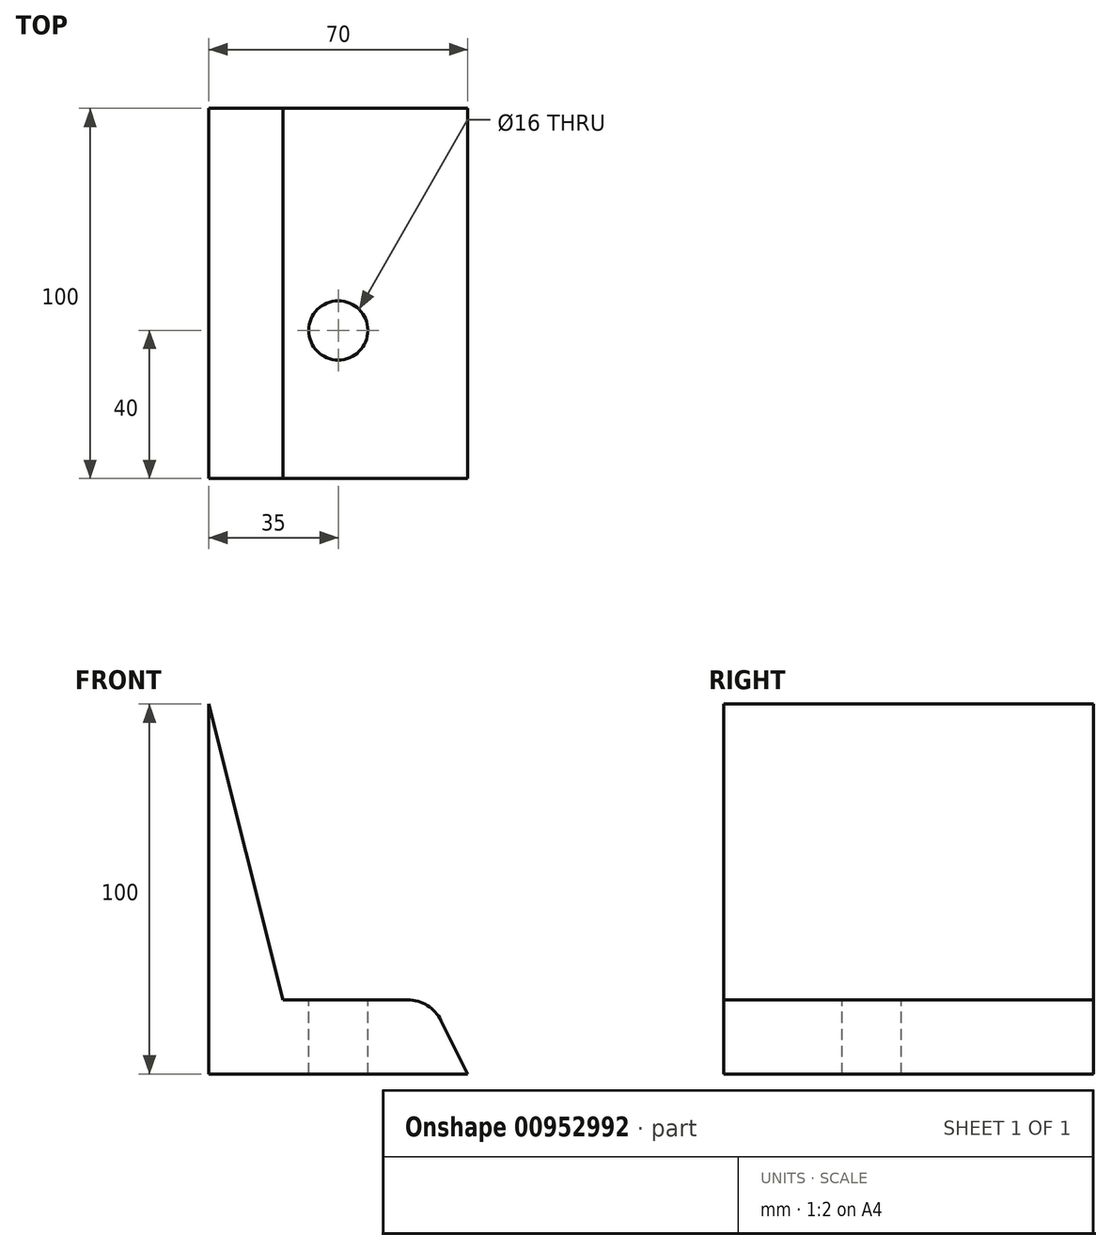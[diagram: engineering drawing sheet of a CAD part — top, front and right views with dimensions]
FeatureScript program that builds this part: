
annotation { "Feature Type Name" : "Feature", "Feature Type Description" : "" }
export const myFeature = defineFeature(function(context is Context, id is Id, definition is map)
    precondition{}
    {
        {
            var Q0;
            Q0=qCreatedBy(makeId("Front.planeOp"),FACE);
            var sketch = newSketch(context, id + "F0", { "sketchPlane" : qUnion([Q0])});
            skLineSegment(sketch, "E0", {"start": v(0, 0) * mm, "end": v(0, 100) * mm});
            skLineSegment(sketch, "E1", {"start": v(0, 100) * mm, "end": v(20, 20) * mm});
            skLineSegment(sketch, "E2", {"start": v(20, 20) * mm, "end": v(60, 20) * mm});
            skLineSegment(sketch, "E3", {"start": v(60, 20) * mm, "end": v(70, 0) * mm});
            skLineSegment(sketch, "E4", {"start": v(70, 0) * mm, "end": v(0, 0) * mm});
            skSolve(sketch);
        }
        {
            var Q0;
            Q0 = qSketchRegion(id + "F0", true);
            extrude(context, id + "F1", {"entities" : qUnion([Q0]), "oppositeDirection" : true, "depth" : 100 * mm, "offsetDistance" : 25 * mm});
        }
        {
            var Q0;
            Q0=makeQuery(id+"F1.opExtrude","SWEPT_EDGE",EDGE,{"disambiguationData":[OSD([sQuery(id+"F0.wireOp",EDGE,"E2"),sQuery(id+"F0.wireOp",EDGE,"E3")])]});
            fillet(context, id + "F2", {"entities" : qUnion([Q0]), "radius" : 10 * mm, "tangentPropagation" : true, "allowEdgeOverflow" : false});
        }
        {
            var Q0;
            Q0=makeQuery(id+"F1.opExtrude","SWEPT_FACE",FACE,{"disambiguationData":[OSD([sQuery(id+"F0.wireOp",EDGE,"E2")])]});
            var sketch = newSketch(context, id + "F3", { "sketchPlane" : qUnion([Q0])});
            skCircle(sketch, "E5", {"center": v(35, 40) * mm, "radius": 8 * mm});
            skSolve(sketch);
        }
        {
            var Q0;
            Q0 = qSketchRegion(id + "F3", true);
            extrude(context, id + "F4", {"entities" : qUnion([Q0]), "operationType" : NewBodyOperationType.REMOVE, "endBound" : BoundingType.THROUGH_ALL, "oppositeDirection" : true, "depth" : 25 * mm, "offsetDistance" : 25 * mm});
        }
    });
